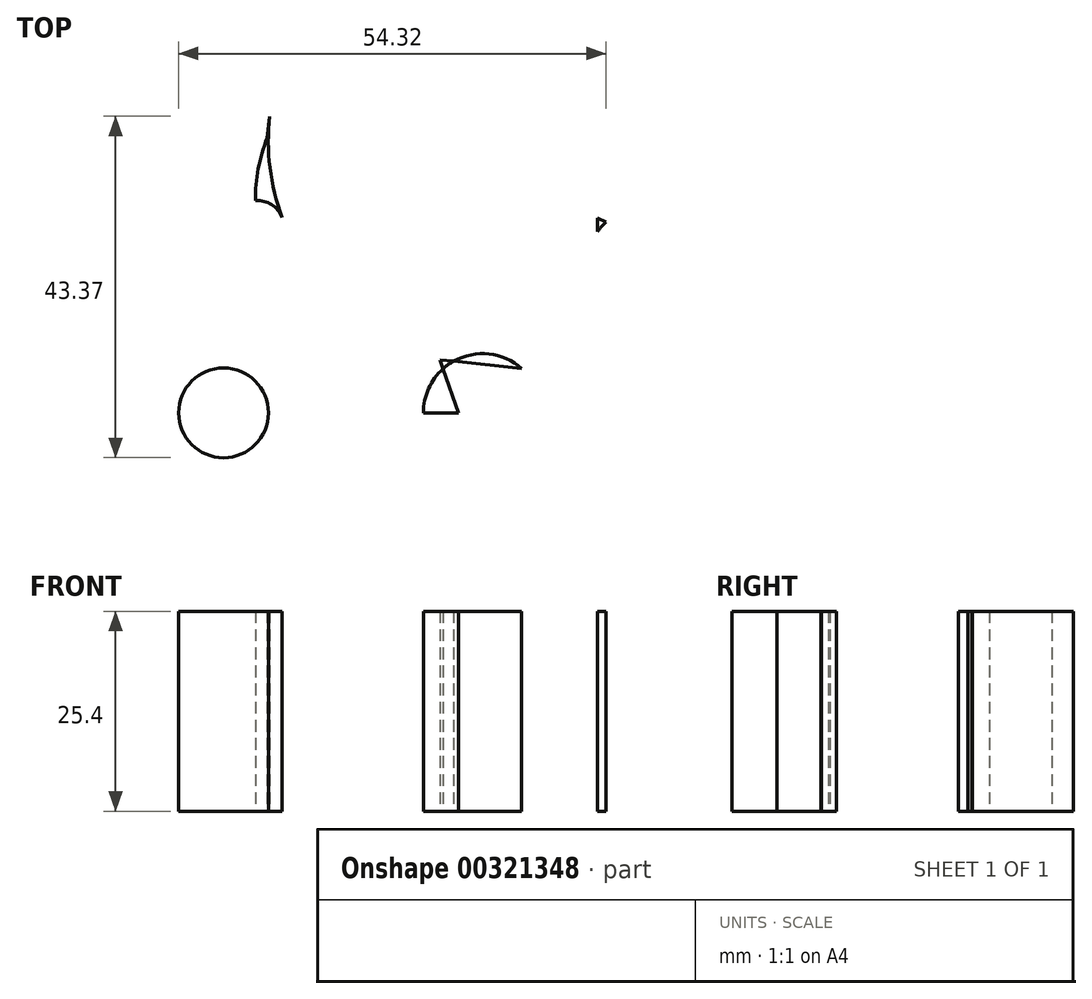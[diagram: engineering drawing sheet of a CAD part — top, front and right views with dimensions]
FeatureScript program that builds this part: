
annotation { "Feature Type Name" : "Feature", "Feature Type Description" : "" }
export const myFeature = defineFeature(function(context is Context, id is Id, definition is map)
    precondition{}
    {
        {
            var Q0;
            Q0=qCreatedBy(makeId("Top.planeOp"),FACE);
            var sketch = newSketch(context, id + "F0", { "sketchPlane" : qUnion([Q0])});
            skLineSegment(sketch, "E0.top", {"start": v(-15.57, -210.46) * mm, "end": v(-0.4, -210.46) * mm});
            skLineSegment(sketch, "E0.right", {"start": v(41.41, -185.7) * mm, "end": v(41.41, -187.44) * mm});
            skArc(sketch, "E1", {"start": v(41.41, -185.7) * mm, "mid": v(40.95, -183.22) * mm, "end": v(40.28, -180.79) * mm});
            skArc(sketch, "E2", {"start": v(27.01, -160.93) * mm, "mid": v(25.4, -160.54) * mm, "end": v(23.77, -160.28) * mm});
            skPoint(sketch, "E3.start.orphan", {"position": v(41.41, -185.7) * mm});
            skPoint(sketch, "E4.orphan", {"position": v(41.41, -160.93) * mm});
            skArc(sketch, "E5", {"start": v(23.77, -160.28) * mm, "mid": v(24.04, -162.36) * mm, "end": v(25.53, -163.84) * mm});
            skPoint(sketch, "E6.orphan", {"position": v(27.01, -160.93) * mm});
            skArc(sketch, "E7", {"start": v(34.33, -210.46) * mm, "mid": v(26.8, -202.94) * mm, "end": v(19.29, -210.46) * mm});
            skLineSegment(sketch, "E8.trimOffspring", {"start": v(12.92, -160.93) * mm, "end": v(15.7, -160.93) * mm});
            skPoint(sketch, "E9.orphan", {"position": v(-15.57, -160.93) * mm});
            skLineSegment(sketch, "E10", {"start": v(40.28, -180.79) * mm, "end": v(41.41, -180.79) * mm});
            skPoint(sketch, "E10.endSnap0", {"position": v(41.41, -198.08) * mm});
            skLineSegment(sketch, "E11", {"start": v(41.41, -185.7) * mm, "end": v(42.5, -186.2) * mm});
            skPoint(sketch, "E12.MirrorP", {"position": v(2.73, -144.45) * mm});
            skArc(sketch, "E13.MirrorCS", {"start": v(-2.04, -183.51) * mm, "mid": v(0, -184) * mm, "end": v(1.32, -185.64) * mm});
            skLineSegment(sketch, "E14.MirrorCS", {"start": v(-0.26, -172.8) * mm, "end": v(-0.55, -175.55) * mm});
            skLineSegment(sketch, "E15.MirrorCS", {"start": v(21.39, -203.72) * mm, "end": v(33.7, -205.02) * mm});
            skArc(sketch, "E16.MirrorCS", {"start": v(-1.73, -186.8) * mm, "mid": v(-1.95, -185.16) * mm, "end": v(-2.04, -183.51) * mm});
            skPoint(sketch, "E17.MirrorP", {"position": v(33.7, -205.02) * mm});
            skArc(sketch, "E18.MirrorC", {"start": v(46.76, -199.27) * mm, "mid": v(43.75, -198.28) * mm, "end": v(41.41, -196.14) * mm});
            skLineSegment(sketch, "E19.MirrorCS", {"start": v(16.63, -202.08) * mm, "end": v(16.51, -203.2) * mm});
            skLineSegment(sketch, "E20.MirrorCS", {"start": v(21.39, -203.72) * mm, "end": v(26.33, -217.96) * mm});
            skPoint(sketch, "E21.MirrorP", {"position": v(-3.24, -201.13) * mm});
            skArc(sketch, "E22.MirrorCS", {"start": v(21.39, -203.72) * mm, "mid": v(18.97, -203) * mm, "end": v(16.63, -202.08) * mm});
            skPoint(sketch, "E23.MirrorP", {"position": v(-1.73, -186.8) * mm});
            skPoint(sketch, "E24.MirrorP", {"position": v(21.39, -203.72) * mm});
            skLineSegment(sketch, "E25.MirrorCS", {"start": v(42.09, -243.64) * mm, "end": v(40.6, -250.02) * mm});
            skArc(sketch, "E26.MirrorCS", {"start": v(-1.73, -186.8) * mm, "mid": v(-1.93, -181.1) * mm, "end": v(-0.55, -175.55) * mm});
            skLineSegment(sketch, "E27.MirrorCS", {"start": v(-15.57, -210.46) * mm, "end": v(-11.8, -210.46) * mm});
            skCircle(sketch, "E28.MirrorC", {"center": v(-6.1, -210.46) * mm, "radius": 5.7 * mm});
            skArc(sketch, "E29.MirrorC", {"start": v(34.33, -210.46) * mm, "mid": v(33.66, -207.36) * mm, "end": v(31.78, -204.81) * mm});
            skLineSegment(sketch, "E30.MirrorCS", {"start": v(21.39, -203.72) * mm, "end": v(23.72, -210.46) * mm});
            skLineSegment(sketch, "E31.MirrorCS", {"start": v(-291.05, -182.48) * mm, "end": v(-302.11, -192.43) * mm});
            skPoint(sketch, "E32.visualSharp", {"position": v(-302.11, -192.43) * mm});
            skArc(sketch, "E32.filletArc", {"start": v(-291.05, -182.48) * mm, "mid": v(-292.8, -189.25) * mm, "end": v(-287.27, -193.53) * mm});
            skPoint(sketch, "E33.orphan", {"position": v(34.97, -242.89) * mm});
            skPoint(sketch, "E34.MirrorCS.end.orphan", {"position": v(41.1, -253.13) * mm});
            skPoint(sketch, "E35.orphan", {"position": v(78.95, -203.3) * mm});
            skPoint(sketch, "E36.MirrorCS.start.orphan", {"position": v(51.98, -149.64) * mm});
            skPoint(sketch, "E37.orphan", {"position": v(27.35, -147.05) * mm});
            skPoint(sketch, "E38.MirrorCS.end.orphan", {"position": v(-15.57, -210.46) * mm});
            skPoint(sketch, "E38.MirrorCS.start.orphan", {"position": v(-15.57, -185.7) * mm});
            skPoint(sketch, "E39.orphan", {"position": v(18.53, -184.04) * mm});
            skLineSegment(sketch, "E40.trimOffspring", {"start": v(19.29, -210.46) * mm, "end": v(26.8, -210.46) * mm});
            skPoint(sketch, "E41.MirrorCS.end.orphan", {"position": v(-147.34, -203.82) * mm});
            skPoint(sketch, "E42.start.orphan", {"position": v(-232.71, -103.47) * mm});
            skPoint(sketch, "E43.end.orphan", {"position": v(-232.71, -97.47) * mm});
            skPoint(sketch, "E43.start.orphan", {"position": v(-264.32, -72.95) * mm});
            skPoint(sketch, "E44.end.orphan", {"position": v(-257.24, -72.95) * mm});
            skLineSegment(sketch, "E45.trimOffspring", {"start": v(-6.1, -210.46) * mm, "end": v(-0.4, -210.46) * mm});
            skArc(sketch, "E46.trimOffspring", {"start": v(1.32, -185.64) * mm, "mid": v(-0.2, -179.3) * mm, "end": v(-0.26, -172.8) * mm});
            skPoint(sketch, "E47.orphan", {"position": v(22.14, -180.79) * mm});
            skLineSegment(sketch, "E48.trimOffspring", {"start": v(41.41, -205.83) * mm, "end": v(46.02, -206.31) * mm});
            skArc(sketch, "E49.trimOffspring", {"start": v(41.41, -187.44) * mm, "mid": v(41.93, -186.8) * mm, "end": v(42.5, -186.2) * mm});
            skPoint(sketch, "E50.start.orphan", {"position": v(78.95, -210.46) * mm});
            skPoint(sketch, "E51.end.orphan", {"position": v(88.49, -210.46) * mm});
            skLineSegment(sketch, "E52.trimOffspring", {"start": v(41.41, -196.14) * mm, "end": v(41.41, -198.08) * mm});
            skLineSegment(sketch, "E53.trimOffspring", {"start": v(41.41, -205.83) * mm, "end": v(41.41, -210.46) * mm});
            skLineSegment(sketch, "E54.trimOffspring", {"start": v(41.41, -196.14) * mm, "end": v(41.41, -210.46) * mm});
            skArc(sketch, "E55.trimOffspring", {"start": v(23.13, -203.9) * mm, "mid": v(20.32, -206.66) * mm, "end": v(19.29, -210.46) * mm});
            skSolve(sketch);
        }
        {
            var Q0;
            Q0 = qSketchRegion(id + "F0", true);
            extrude(context, id + "F1", {"entities" : qUnion([Q0]), "depth" : 25.4 * mm});
        }
    });
